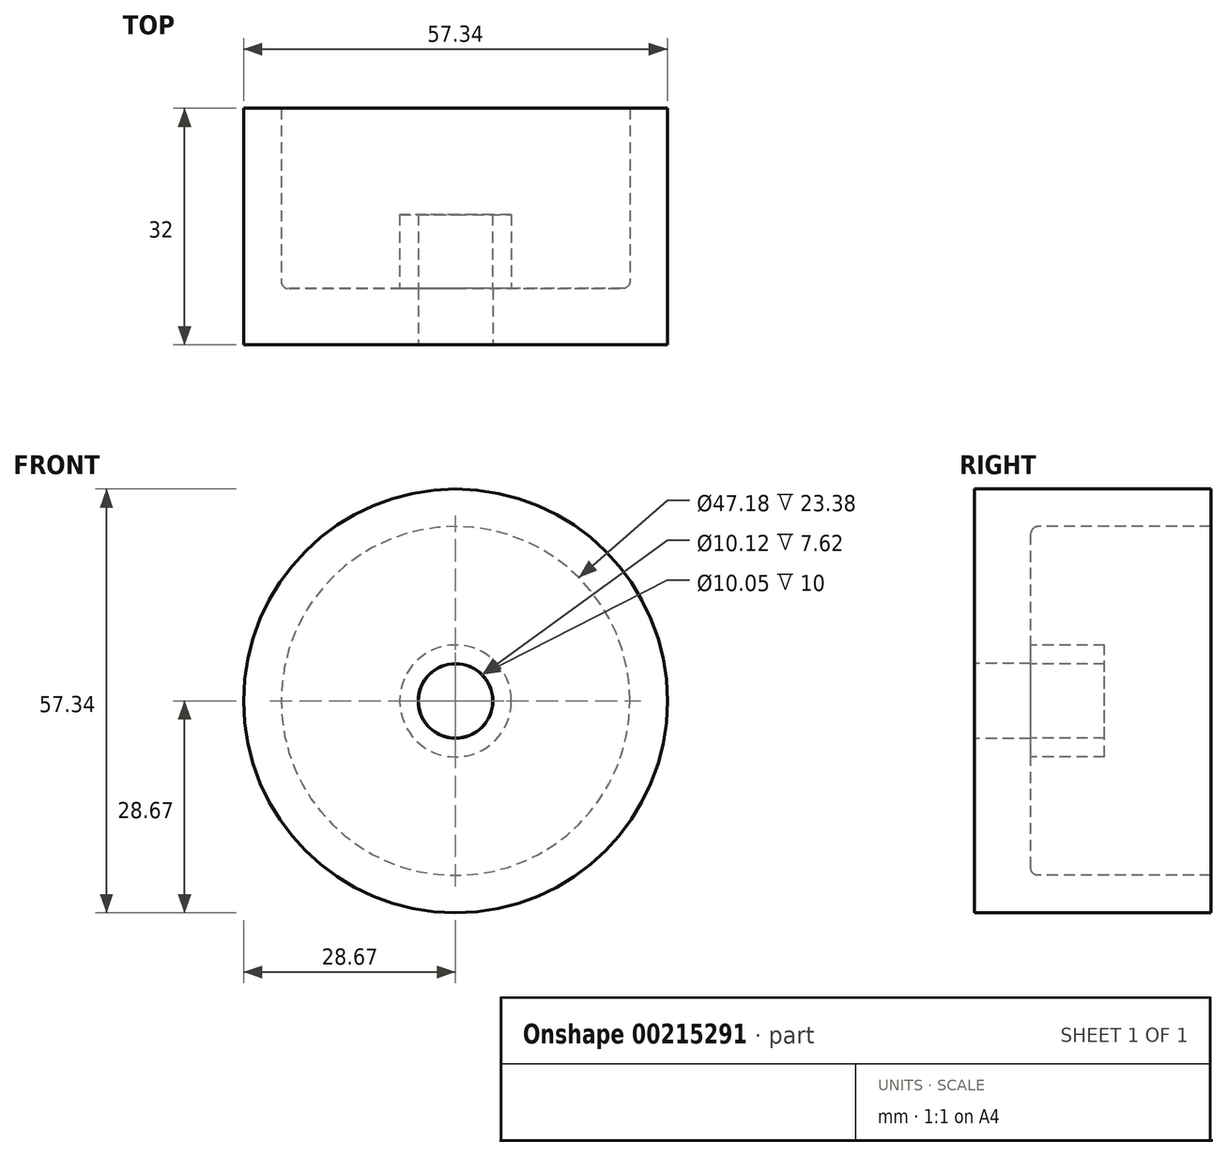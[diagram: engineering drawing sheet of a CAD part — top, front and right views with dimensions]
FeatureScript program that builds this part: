
annotation { "Feature Type Name" : "Feature", "Feature Type Description" : "" }
export const myFeature = defineFeature(function(context is Context, id is Id, definition is map)
    precondition{}
    {
        {
            var Q0;
            Q0=qCreatedBy(makeId("Right.planeOp"),FACE);
            var sketch = newSketch(context, id + "F0", { "sketchPlane" : qUnion([Q0])});
            skLineSegment(sketch, "E0", {"start": v(0, 5.06) * mm, "end": v(0, 28.67) * mm});
            skLineSegment(sketch, "E1", {"start": v(0, 28.67) * mm, "end": v(32, 28.67) * mm});
            skLineSegment(sketch, "E2", {"start": v(32, 28.67) * mm, "end": v(32, 23.6) * mm});
            skLineSegment(sketch, "E3", {"start": v(32, 23.6) * mm, "end": v(8.62, 23.6) * mm});
            skLineSegment(sketch, "E4", {"start": v(7.62, 22.6) * mm, "end": v(7.62, 7.56) * mm});
            skLineSegment(sketch, "E5", {"start": v(7.62, 7.56) * mm, "end": v(17.62, 7.56) * mm});
            skLineSegment(sketch, "E6", {"start": v(17.62, 7.56) * mm, "end": v(17.62, 5.02) * mm});
            skLineSegment(sketch, "E7", {"start": v(17.62, 5.02) * mm, "end": v(7.62, 5.02) * mm});
            skLineSegment(sketch, "E8", {"start": v(7.62, 5.06) * mm, "end": v(7.62, 5.02) * mm});
            skLineSegment(sketch, "E9", {"start": v(7.62, 5.06) * mm, "end": v(0, 5.06) * mm});
            skPoint(sketch, "E10.visualSharp", {"position": v(7.62, 23.6) * mm});
            skArc(sketch, "E10.filletArc", {"start": v(8.62, 23.6) * mm, "mid": v(7.91, 23.3) * mm, "end": v(7.62, 22.6) * mm});
            skLineSegment(sketch, "E11", {"start": v(-75.56, 0) * mm, "end": v(74.23, 0) * mm, "construction": true});
            skSolve(sketch);
        }
        {
            var Q0;
            Q0=qSketchRegion(id+"F0",true);
            var Q1;
            Q1=sQuery(id+"F0.wireOp",EDGE,"E11");
            revolve(context, id + "F1", {"entities" : qUnion([Q0]), "axis" : qUnion([Q1]), "revolveType" : RevolveType.FULL});
        }
    });
